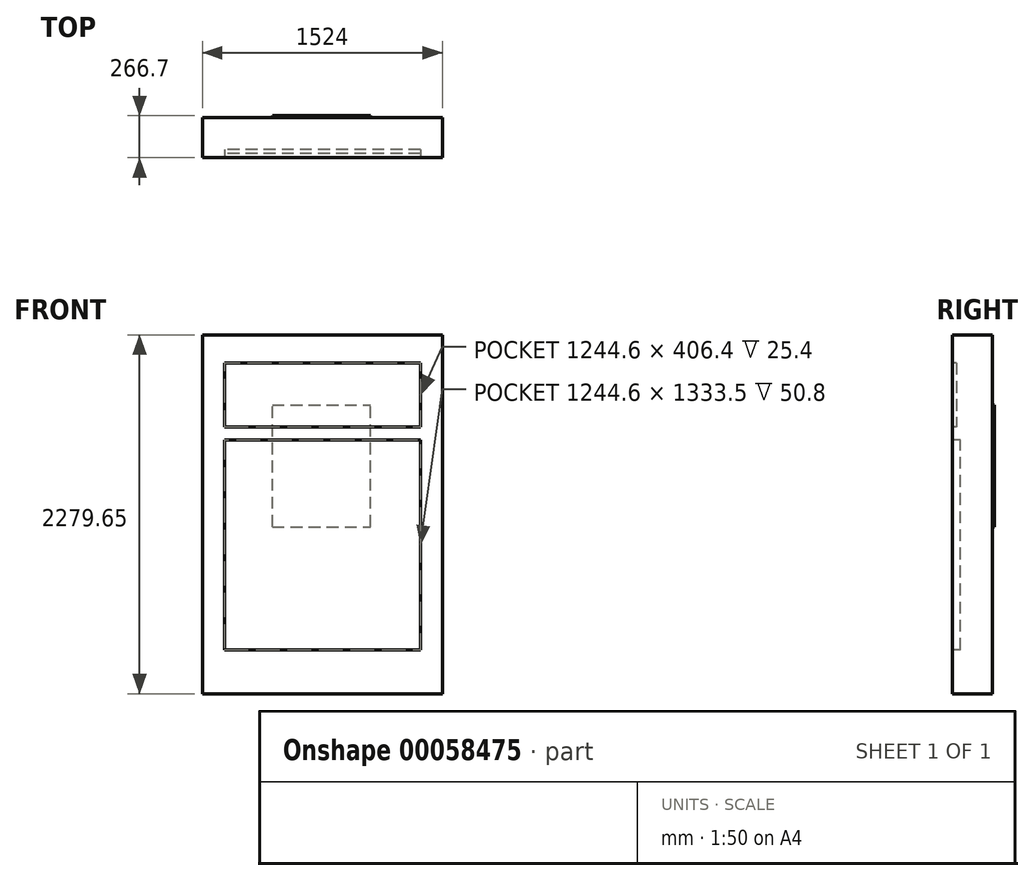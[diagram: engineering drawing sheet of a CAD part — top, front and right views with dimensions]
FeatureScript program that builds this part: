
annotation { "Feature Type Name" : "Feature", "Feature Type Description" : "" }
export const myFeature = defineFeature(function(context is Context, id is Id, definition is map)
    precondition{}
    {
        {
            var Q0;
            Q0=qCreatedBy(makeId("Front.planeOp"),FACE);
            var sketch = newSketch(context, id + "F0", { "sketchPlane" : qUnion([Q0])});
            skLineSegment(sketch, "E0.bottom", {"start": v(0, 0) * mm, "end": v(1524, 0) * mm});
            skLineSegment(sketch, "E0.top", {"start": v(0, -2279.65) * mm, "end": v(1524, -2279.65) * mm});
            skLineSegment(sketch, "E0.left", {"start": v(0, 0) * mm, "end": v(0, -2279.65) * mm});
            skLineSegment(sketch, "E0.right", {"start": v(1524, 0) * mm, "end": v(1524, -2279.65) * mm});
            skSolve(sketch);
        }
        {
            var Q0;
            Q0 = qSketchRegion(id + "F0", true);
            extrude(context, id + "F1", {"entities" : qUnion([Q0]), "depth" : 254 * mm});
        }
        {
            var Q0;
            Q0=makeQuery(id+"F1.opExtrude","CAP_FACE",FACE,{"disambiguationData":[OSD([sQuery(id+"F0.wireOp",EDGE,"E0.bottom"),sQuery(id+"F0.wireOp",EDGE,"E0.top"),sQuery(id+"F0.wireOp",EDGE,"E0.left"),sQuery(id+"F0.wireOp",EDGE,"E0.right")])],"isStart":false});
            var sketch = newSketch(context, id + "F2", { "sketchPlane" : qUnion([Q0])});
            skLineSegment(sketch, "E1.rect.bottom", {"start": v(1384.3, -177.8) * mm, "end": v(139.7, -177.8) * mm});
            skLineSegment(sketch, "E1.rect.top", {"start": v(1384.3, -584.2) * mm, "end": v(139.7, -584.2) * mm});
            skLineSegment(sketch, "E1.rect.left", {"start": v(1384.3, -177.8) * mm, "end": v(1384.3, -584.2) * mm});
            skLineSegment(sketch, "E1.rect.right", {"start": v(139.7, -177.8) * mm, "end": v(139.7, -584.2) * mm});
            skPoint(sketch, "E1.rect.middle", {"position": v(762, -381) * mm});
            skSolve(sketch);
        }
        {
            var Q0;
            Q0=makeQuery(id+"F2.imprint","IMPRINT",FACE,{"disambiguationData":[TD([[makeQuery(id+"F2.imprint","IMPRINT",EDGE,{"derivedFrom":sQuery(id+"F2.wireOp",EDGE,"E1.rect.bottom")}),1.0]])]});
            extrude(context, id + "F3", {"entities" : qUnion([Q0]), "operationType" : NewBodyOperationType.REMOVE, "oppositeDirection" : true, "depth" : 25.4 * mm});
        }
        {
            var Q0;
            Q0=makeQuery(id+"F1.opExtrude","CAP_FACE",FACE,{"disambiguationData":[OSD([sQuery(id+"F0.wireOp",EDGE,"E0.bottom"),sQuery(id+"F0.wireOp",EDGE,"E0.top"),sQuery(id+"F0.wireOp",EDGE,"E0.left"),sQuery(id+"F0.wireOp",EDGE,"E0.right")])],"isStart":false});
            var sketch = newSketch(context, id + "F4", { "sketchPlane" : qUnion([Q0])});
            skLineSegment(sketch, "E2.rect.bottom", {"start": v(1384.3, -2000.25) * mm, "end": v(139.7, -2000.25) * mm});
            skLineSegment(sketch, "E2.rect.top", {"start": v(1384.3, -666.75) * mm, "end": v(139.7, -666.75) * mm});
            skLineSegment(sketch, "E2.rect.left", {"start": v(1384.3, -2000.25) * mm, "end": v(1384.3, -666.75) * mm});
            skLineSegment(sketch, "E2.rect.right", {"start": v(139.7, -2000.25) * mm, "end": v(139.7, -666.75) * mm});
            skPoint(sketch, "E2.rect.middle", {"position": v(762, -1333.5) * mm});
            skPoint(sketch, "E2.rect.middle.positionSnap0", {"position": v(762, -2279.65) * mm});
            skPoint(sketch, "E2.rect.centerSnap0", {"position": v(762, -2279.65) * mm});
            skSolve(sketch);
        }
        {
            var Q0;
            Q0 = qSketchRegion(id + "F4", true);
            extrude(context, id + "F5", {"entities" : qUnion([Q0]), "operationType" : NewBodyOperationType.REMOVE, "oppositeDirection" : true, "depth" : 50.8 * mm});
        }
        {
            var Q0;
            Q0=makeQuery(id+"F1.opExtrude","CAP_FACE",FACE,{"disambiguationData":[OSD([sQuery(id+"F0.wireOp",EDGE,"E0.bottom"),sQuery(id+"F0.wireOp",EDGE,"E0.top"),sQuery(id+"F0.wireOp",EDGE,"E0.left"),sQuery(id+"F0.wireOp",EDGE,"E0.right")])],"isStart":true});
            var sketch = newSketch(context, id + "F6", { "sketchPlane" : qUnion([Q0])});
            skLineSegment(sketch, "E3.rect.bottom", {"start": v(-444.5, -1219.2) * mm, "end": v(-1066.8, -1219.2) * mm});
            skLineSegment(sketch, "E3.rect.top", {"start": v(-444.5, -444.5) * mm, "end": v(-1066.8, -444.5) * mm});
            skLineSegment(sketch, "E3.rect.left", {"start": v(-444.5, -1219.2) * mm, "end": v(-444.5, -444.5) * mm});
            skLineSegment(sketch, "E3.rect.right", {"start": v(-1066.8, -1219.2) * mm, "end": v(-1066.8, -444.5) * mm});
            skPoint(sketch, "E3.rect.middle", {"position": v(-755.65, -831.85) * mm});
            skSolve(sketch);
        }
        {
            var Q0;
            Q0 = qSketchRegion(id + "F6", true);
            extrude(context, id + "F7", {"entities" : qUnion([Q0]), "operationType" : NewBodyOperationType.ADD, "depth" : 12.7 * mm});
        }
    });
